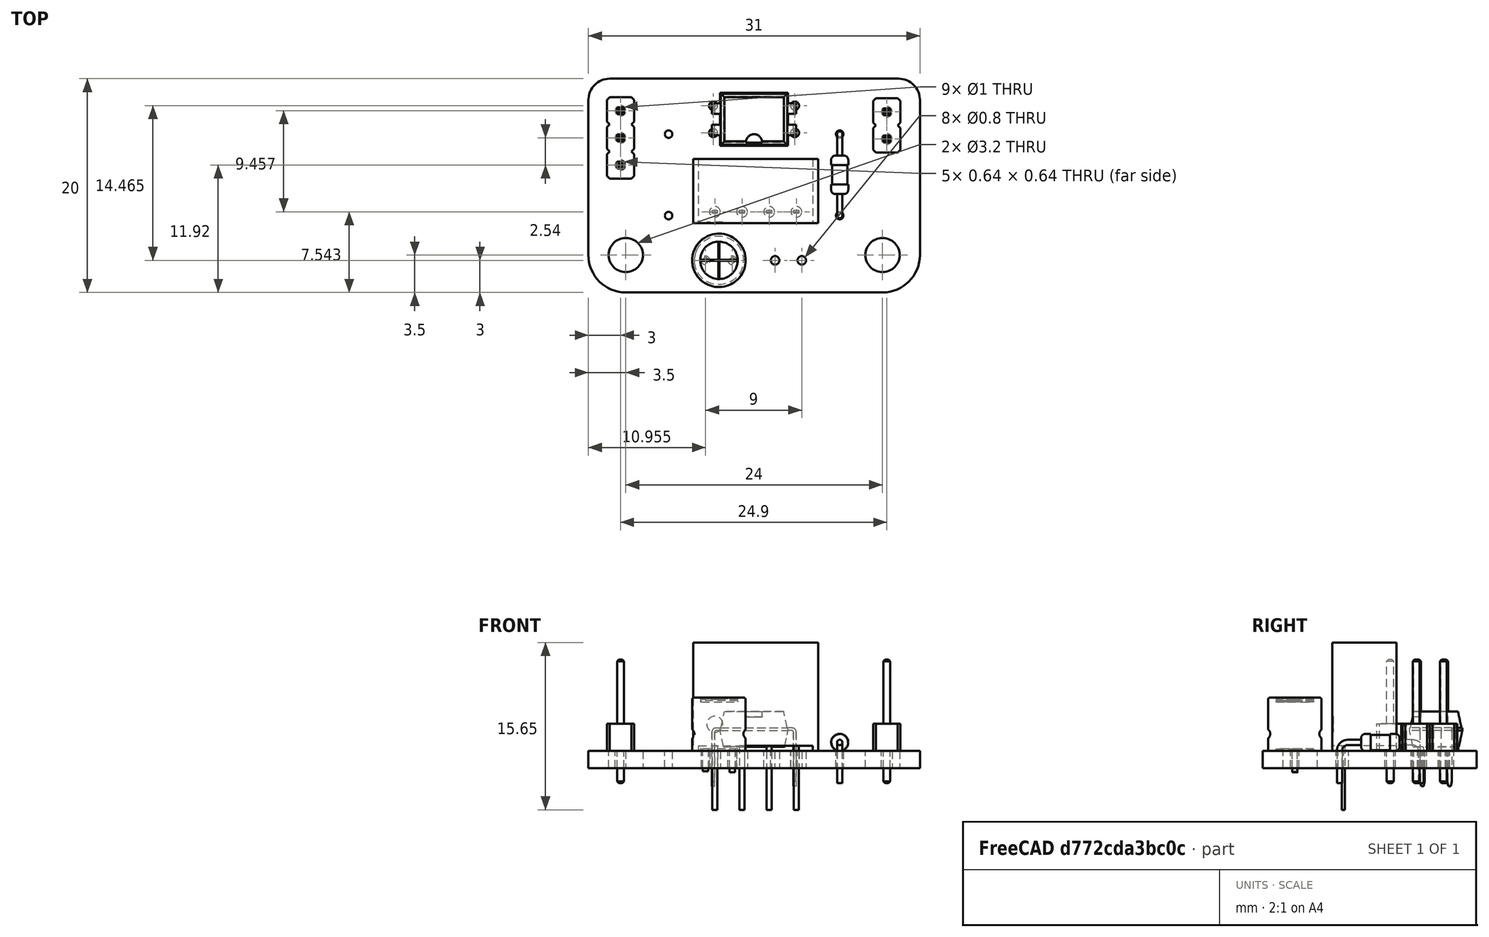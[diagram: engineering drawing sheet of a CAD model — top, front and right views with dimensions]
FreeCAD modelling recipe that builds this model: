
FCSTD DOCUMENT  (FreeCAD 1.0R39109 (Git))
Label: isolated_probe_pcb
License: All rights reserved
LicenseURL: http://en.wikipedia.org/wiki/All_rights_reserved
objects: Part::Feature×7, App::Part×4, App::Link×2, PartDesign::CoordinateSystem×1, Sketcher::SketchObject×1
note: 10 computed .brp shape members not serialized (recipe doc carries the construction recipe); baked Part::Feature solids carry a one-line shape summary decoded from their .brp

FEATURE [PartDesign::CoordinateSystem] Local_CS_7017
  AttacherType = Attacher::AttachEngine3D
  MapMode = 2
FEATURE [Part::Feature] Pcb_7017
  Placement = pos=(-151,98,0) rot=(0,0,1;0rad)
  shape: bbox 31 x 20 x 1.6 mm, 33 faces (baked)
FEATURE [Sketcher::SketchObject] PCB_Sketch_7017
  ArcFitTolerance = 1e-06
  FullyConstrained = false
  MakeInternals = false
  sketch-geometry (8):
    g0: LineSegment StartX=30 StartY=-1 StartZ=0 EndX=3 EndY=-1 EndZ=0
    g1: LineSegment StartX=32 StartY=-17.5 StartZ=0 EndX=32 EndY=-3 EndZ=0
    g2: LineSegment StartX=1 StartY=-3 StartZ=0 EndX=1 EndY=-17.5 EndZ=0
    g3: LineSegment StartX=28.5 StartY=-21 StartZ=0 EndX=4.5 EndY=-21 EndZ=0
    g4: ArcOfCircle CenterX=30 CenterY=-3 CenterZ=0 NormalX=0 NormalY=0 NormalZ=-1 AngleXU=1.5708 Radius=2 StartAngle=0 EndAngle=1.5708
    g5: ArcOfCircle CenterX=4.5 CenterY=-17.5 CenterZ=0 NormalX=0 NormalY=0 NormalZ=-1 AngleXU=-1.5708 Radius=3.5 StartAngle=0 EndAngle=1.5708
    g6: ArcOfCircle CenterX=3 CenterY=-3 CenterZ=0 NormalX=0 NormalY=0 NormalZ=-1 AngleXU=-7.47076e-07 Radius=2 StartAngle=0 EndAngle=1.5708
    g7: ArcOfCircle CenterX=28.5 CenterY=-17.5 CenterZ=0 NormalX=0 NormalY=0 NormalZ=-1 AngleXU=3.14159 Radius=3.5 StartAngle=0 EndAngle=1.5708
  constraints (8):
    c: Coincident(g2,g5)
    c: Coincident(g2,g6)
    c: Coincident(g0,g6)
    c: Coincident(g3,g5)
    c: Coincident(g3,g7)
    c: Coincident(g0,g4)
    c: Coincident(g1,g7)
    c: Coincident(g1,g4)
FEATURE [App::Part] Board_Geoms_7017
  Group = -> [Pcb_7017,PCB_Sketch_7017]
  Origin = -> Origin
FEATURE [Part::Feature] Shape  label="C1_CP_Radial_D50mm_P250mm_05f78be0c50b"
  Placement = pos=(14.4551,-18,0) rot=(0,0,1;3.14159rad)
  shape: bbox 6.128 x 6.515 x 7 mm, 49 faces (baked)
FEATURE [Part::Feature] Shape001  label="U1_B0505S-1W_e112f722edd0"
  Placement = pos=(12.8325,-13.4575,0) rot=(0,0,1;1.5708rad)
  shape: bbox 11.68 x 6 x 15.65 mm, 32 faces (baked)
FEATURE [Part::Feature] Shape002  label="R2_R_Axial_DIN0204_L36mm_D16mm_P762mm_Horizontal_3d6b873543b0"
  Placement = pos=(24.5,-6.19,0) rot=(0,0,-1;1.5708rad)
  shape: bbox 1.732 x 8.285 x 4.666 mm, 17 faces (baked)
FEATURE [Part::Feature] Shape003  label="J1_PinHeader_1x03_P254mm_Vertical_de2919090d28"
  Placement = pos=(4,-9.08,0) rot=(0,0,1;3.14159rad)
  shape: bbox 2.54 x 7.62 x 11.54 mm, 76 faces (baked)
FEATURE [Part::Feature] Shape004  label="U2_DIP-4_W7.62mm_57e4b470440d"
  Placement = pos=(20.3,-6.075,0) rot=(0,0,1;3.14159rad)
  shape: bbox 7.874 x 4.93 x 6.98 mm, 80 faces (baked)
FEATURE [App::Link] R2_R_Axial_DIN0204_L36mm_D16mm_P762mm_Horizontal_3d6b873543b0_ln_  label="R1_R_Axial_DIN0204_L36mm_D16mm_P762mm_Horizontal_5b52c6b7a64e"
  LinkPlacement = pos=(8.5,-6.19,0) rot=(0,0,-1;1.5708rad)
  LinkedObject = -> Shape002
  Placement = pos=(8.5,-6.19,0) rot=(0,0,-1;1.5708rad)
FEATURE [Part::Feature] Shape005  label="J2_PinHeader_1x02_P254mm_Vertical_7ebff6164e3d"
  Placement = pos=(28.9,-4.1,0) rot=(0,0,1;0rad)
  shape: bbox 2.54 x 5.08 x 11.54 mm, 52 faces (baked)
FEATURE [App::Link] C1_CP_Radial_D50mm_P250mm_05f78be0c50b_ln_  label="C2_CP_Radial_D50mm_P250mm_face468587a2"
  LinkPlacement = pos=(20.9551,-18,0) rot=(0,0,1;3.14159rad)
  LinkedObject = -> Shape
  Placement = pos=(20.9551,-18,0) rot=(0,0,1;3.14159rad)
FEATURE [App::Part] Top_7017
  Group = -> [Shape,Shape001,Shape002,Shape003,Shape004,R2_R_Axial_DIN0204_L36mm_D16mm_P762mm_Horizontal_3d6b873543b0_ln_,Shape005,C1_CP_Radial_D50mm_P250mm_05f78be0c50b_ln_]
  Origin = -> Origin003
FEATURE [App::Part] Step_Models_7017
  Group = -> [Top_7017]
  Origin = -> Origin002
FEATURE [App::Part] Board_7017  label="isolated_probe"
  Group = -> [Local_CS_7017,Board_Geoms_7017,Step_Models_7017]
  Origin = -> Origin001
